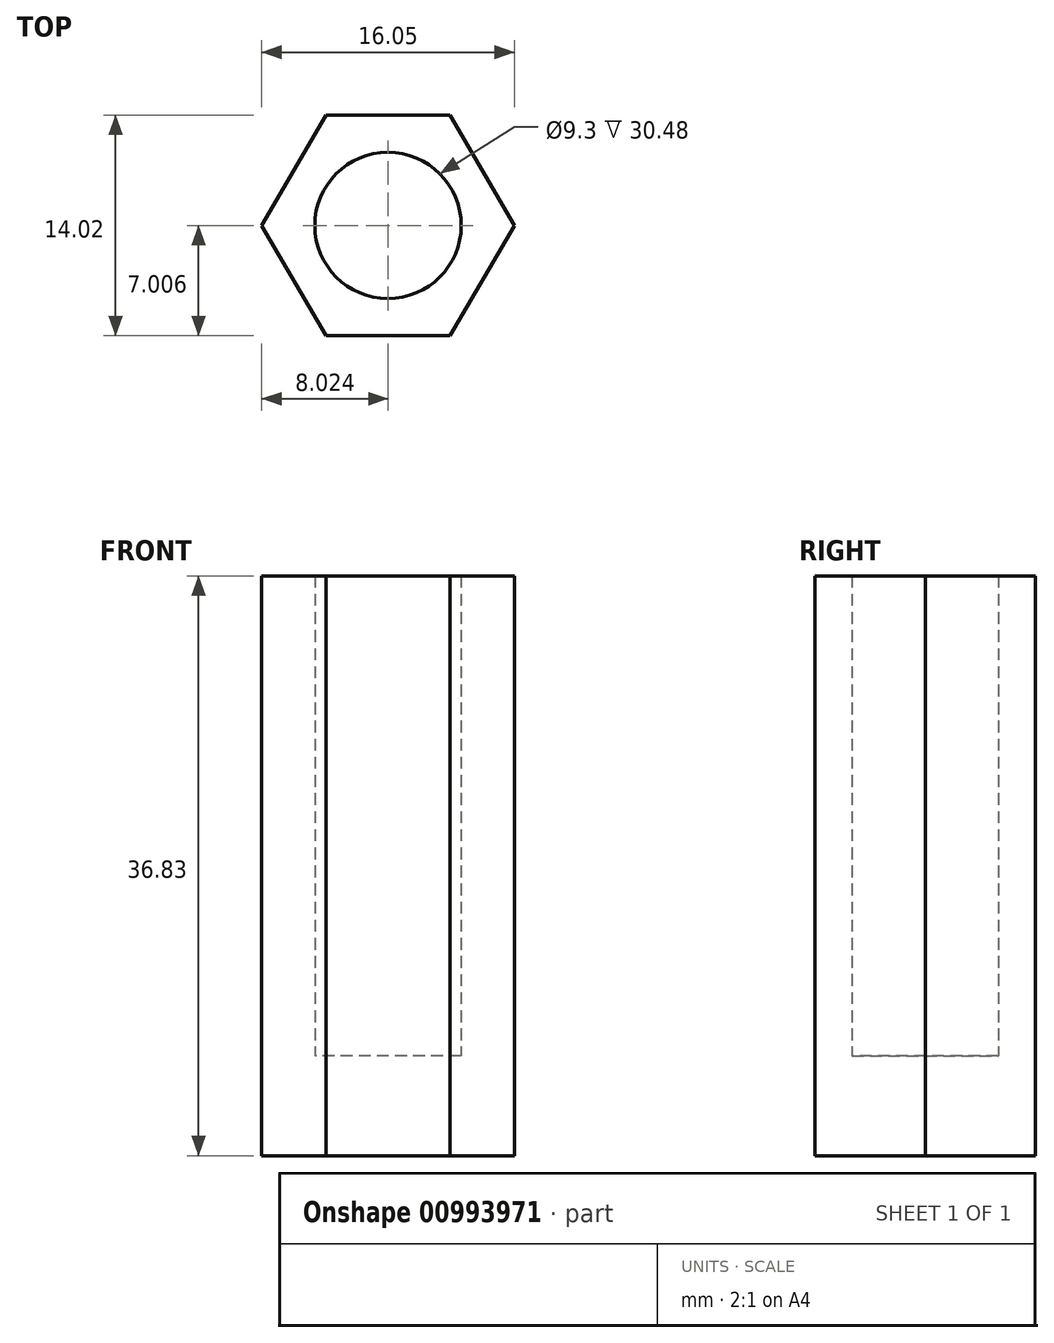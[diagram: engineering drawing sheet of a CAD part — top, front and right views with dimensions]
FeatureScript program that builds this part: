
annotation { "Feature Type Name" : "Feature", "Feature Type Description" : "" }
export const myFeature = defineFeature(function(context is Context, id is Id, definition is map)
    precondition{}
    {
        {
            var Q0;
            Q0=qCreatedBy(makeId("Top.planeOp"),FACE);
            var sketch = newSketch(context, id + "F0", { "sketchPlane" : qUnion([Q0])});
            skLineSegment(sketch, "E0", {"start": v(-8.86, 40.6) * mm, "end": v(-8.86, 26.58) * mm});
            skLineSegment(sketch, "E1", {"start": v(-8.86, 26.58) * mm, "end": v(-8.86, 33.59) * mm});
            skLineSegment(sketch, "E2", {"start": v(-8.86, 33.59) * mm, "end": v(-0.83, 33.59) * mm});
            skLineSegment(sketch, "E3", {"start": v(-0.83, 33.59) * mm, "end": v(-8.86, 33.59) * mm});
            skLineSegment(sketch, "E4", {"start": v(-8.86, 33.59) * mm, "end": v(-16.88, 33.59) * mm});
            skLineSegment(sketch, "E5", {"start": v(-8.86, 40.6) * mm, "end": v(-12.8, 40.6) * mm});
            skLineSegment(sketch, "E6", {"start": v(-12.8, 40.6) * mm, "end": v(-4.92, 40.6) * mm});
            skLineSegment(sketch, "E7", {"start": v(-8.86, 26.58) * mm, "end": v(-4.92, 26.58) * mm});
            skLineSegment(sketch, "E8", {"start": v(-4.92, 26.58) * mm, "end": v(-12.8, 26.58) * mm});
            skLineSegment(sketch, "E9", {"start": v(-12.8, 26.58) * mm, "end": v(-16.88, 33.59) * mm});
            skLineSegment(sketch, "E10", {"start": v(-12.8, 40.6) * mm, "end": v(-16.88, 33.59) * mm});
            skLineSegment(sketch, "E11", {"start": v(-4.92, 40.6) * mm, "end": v(-0.83, 33.59) * mm});
            skLineSegment(sketch, "E12", {"start": v(-4.92, 26.58) * mm, "end": v(-0.83, 33.59) * mm});
            skCircle(sketch, "E13", {"center": v(-8.86, 33.59) * mm, "radius": 4.66 * mm});
            skSolve(sketch);
        }
        {
            var Q0;
            {var subQ0=sQuery(id+"F0.wireOp",EDGE,"E11");Q0=makeQuery(id+"F0.imprint","IMPRINT",FACE,{"disambiguationData":[TD([[makeQuery(id+"F0.imprint","IMPRINT",EDGE,{"derivedFrom":subQ0}),-1.0]])]});}
            var Q1;
            {var subQ0=sQuery(id+"F0.wireOp",EDGE,"E10");Q1=makeQuery(id+"F0.imprint","IMPRINT",FACE,{"disambiguationData":[TD([[makeQuery(id+"F0.imprint","IMPRINT",EDGE,{"derivedFrom":subQ0}),1.0]])]});}
            var Q2;
            {var subQ3=sQuery(id+"F0.wireOp",EDGE,"E9");Q2=makeQuery(id+"F0.imprint","IMPRINT",FACE,{"disambiguationData":[TD([[makeQuery(id+"F0.imprint","IMPRINT",EDGE,{"derivedFrom":subQ3}),-1.0]])]});}
            var Q3;
            {var subQ0=sQuery(id+"F0.wireOp",EDGE,"E12");Q3=makeQuery(id+"F0.imprint","IMPRINT",FACE,{"disambiguationData":[TD([[makeQuery(id+"F0.imprint","IMPRINT",EDGE,{"derivedFrom":subQ0}),1.0]])]});}
            var Q4;
            {var subQ1=sQuery(id+"F0.wireOp",EDGE,"E0");var subQ3=sQuery(id+"F0.wireOp",EDGE,"E13");var subQ4=makeQuery(id+"F0.imprint","INTERSECT",VERTEX,{"derivedFrom":[subQ1,subQ3]});Q4=makeQuery(id+"F0.imprint","IMPRINT",FACE,{"disambiguationData":[TD([[makeQuery(id+"F0.imprint","IMPRINT",EDGE,{"disambiguationData":[TD([[subQ4,-1.0]])],"derivedFrom":subQ3}),1.0]])]});}
            var Q5;
            {var subQ1=sQuery(id+"F0.wireOp",EDGE,"E0");var subQ3=sQuery(id+"F0.wireOp",EDGE,"E13");var subQ4=makeQuery(id+"F0.imprint","INTERSECT",VERTEX,{"derivedFrom":[subQ1,subQ3]});Q5=makeQuery(id+"F0.imprint","IMPRINT",FACE,{"disambiguationData":[TD([[makeQuery(id+"F0.imprint","IMPRINT",EDGE,{"disambiguationData":[TD([[subQ4,1.0]])],"derivedFrom":subQ3}),1.0]])]});}
            var Q6;
            {var subQ1=sQuery(id+"F0.wireOp",EDGE,"E1");var subQ3=sQuery(id+"F0.wireOp",EDGE,"E13");var subQ4=makeQuery(id+"F0.imprint","INTERSECT",VERTEX,{"derivedFrom":[subQ1,subQ3]});Q6=makeQuery(id+"F0.imprint","IMPRINT",FACE,{"disambiguationData":[TD([[makeQuery(id+"F0.imprint","IMPRINT",EDGE,{"disambiguationData":[TD([[subQ4,-1.0]])],"derivedFrom":subQ3}),1.0]])]});}
            var Q7;
            {var subQ1=sQuery(id+"F0.wireOp",EDGE,"E1");var subQ3=sQuery(id+"F0.wireOp",EDGE,"E13");var subQ4=makeQuery(id+"F0.imprint","INTERSECT",VERTEX,{"derivedFrom":[subQ1,subQ3]});Q7=makeQuery(id+"F0.imprint","IMPRINT",FACE,{"disambiguationData":[TD([[makeQuery(id+"F0.imprint","IMPRINT",EDGE,{"disambiguationData":[TD([[subQ4,1.0]])],"derivedFrom":subQ3}),1.0]])]});}
            extrude(context, id + "F1", {"entities" : qUnion([Q0, Q1, Q2, Q3, Q4, Q5, Q6, Q7]), "oppositeDirection" : true, "depth" : 6.35 * mm, "offsetDistance" : 25.4 * mm});
        }
        {
            var Q0;
            Q0=makeQuery(id+"F1.opExtrude","CAP_FACE",FACE,{"disambiguationData":[OSD([sQuery(id+"F0.wireOp",EDGE,"E6"),sQuery(id+"F0.wireOp",EDGE,"E8"),sQuery(id+"F0.wireOp",EDGE,"E9"),sQuery(id+"F0.wireOp",EDGE,"E10"),sQuery(id+"F0.wireOp",EDGE,"E11"),sQuery(id+"F0.wireOp",EDGE,"E12")])],"isStart":true});
            var sketch = newSketch(context, id + "F2", { "sketchPlane" : qUnion([Q0])});
            skLineSegment(sketch, "E14", {"start": v(-16.88, 33.59) * mm, "end": v(-0.83, 33.59) * mm});
            skCircle(sketch, "E15", {"center": v(-8.86, 33.59) * mm, "radius": 4.65 * mm});
            skSolve(sketch);
        }
        {
            var Q0;
            {var subQ0=sQuery(id+"F2.wireOp",EDGE,"E15");var subQ1=sQuery(id+"F2.wireOp",EDGE,"E14");var subQ2=makeQuery(id+"F2.imprint","INTERSECT",VERTEX,{"disambiguationData":[OD(0.0)],"derivedFrom":[subQ1,subQ0]});Q0=makeQuery(id+"F2.imprint","IMPRINT",FACE,{"disambiguationData":[TD([[makeQuery(id+"F2.imprint","IMPRINT",EDGE,{"disambiguationData":[TD([[subQ2,-1.0]])],"derivedFrom":subQ1}),1.0]])]});}
            var Q1;
            {var subQ0=sQuery(id+"F2.wireOp",EDGE,"E15");var subQ1=sQuery(id+"F2.wireOp",EDGE,"E14");var subQ2=makeQuery(id+"F2.imprint","INTERSECT",VERTEX,{"disambiguationData":[OD(0.0)],"derivedFrom":[subQ1,subQ0]});Q1=makeQuery(id+"F2.imprint","IMPRINT",FACE,{"disambiguationData":[TD([[makeQuery(id+"F2.imprint","IMPRINT",EDGE,{"disambiguationData":[TD([[subQ2,-1.0]])],"derivedFrom":subQ1}),-1.0]])]});}
            extrude(context, id + "F3", {"entities" : qUnion([Q0, Q1]), "operationType" : NewBodyOperationType.ADD, "depth" : 30.48 * mm, "offsetDistance" : 25.4 * mm});
        }
    });
